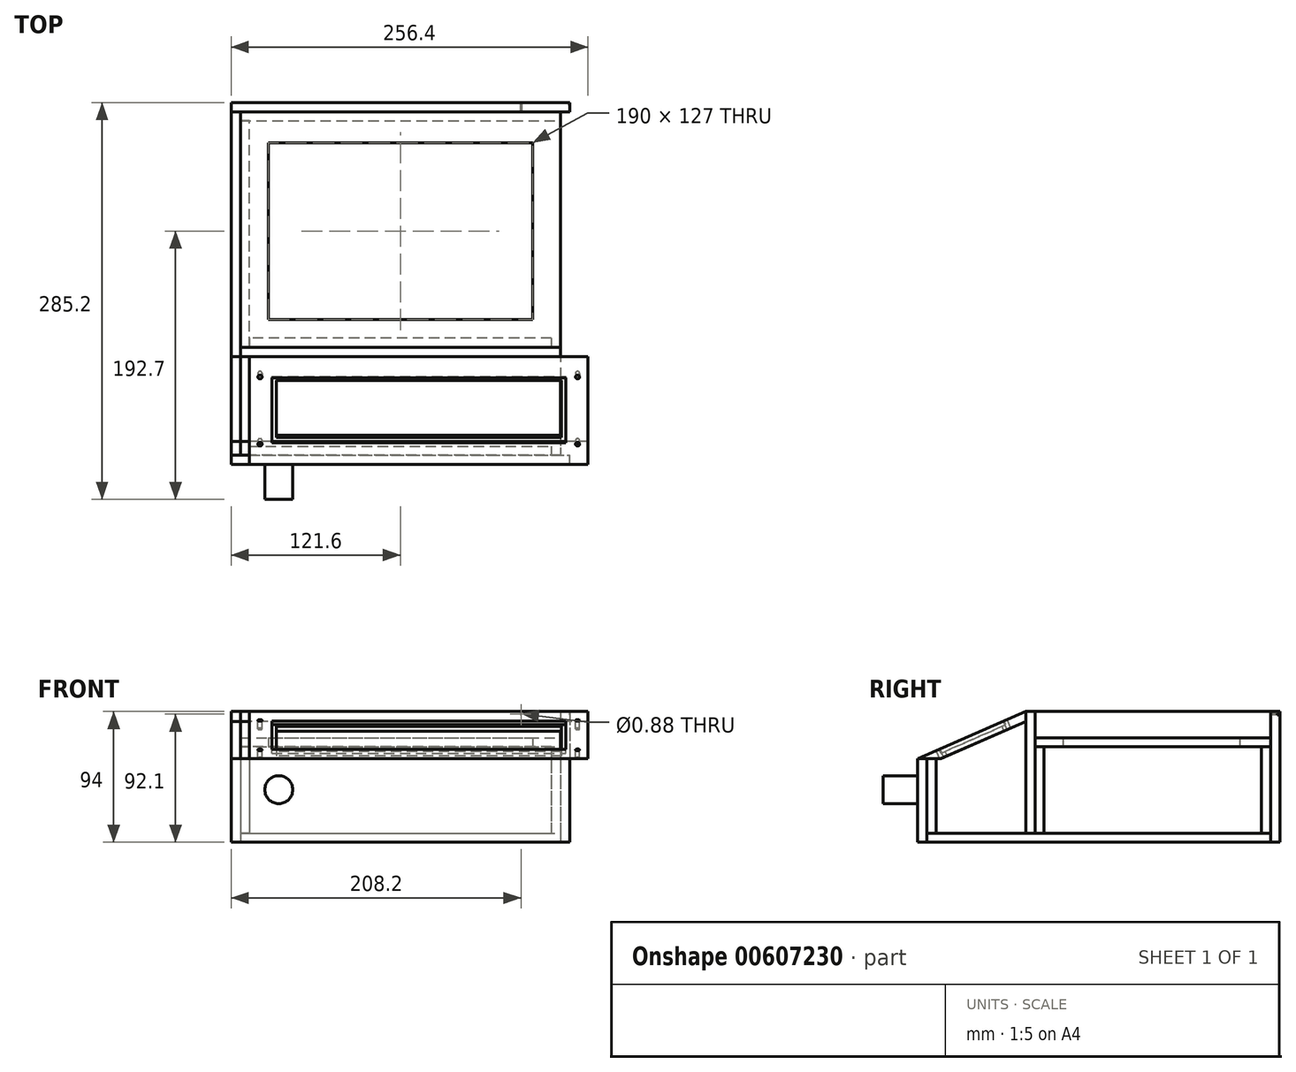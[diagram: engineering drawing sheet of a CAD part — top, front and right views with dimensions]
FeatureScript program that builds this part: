
annotation { "Feature Type Name" : "Feature", "Feature Type Description" : "" }
export const myFeature = defineFeature(function(context is Context, id is Id, definition is map)
    precondition{}
    {
        {
            var Q0;
            Q0=qCreatedBy(makeId("Top.planeOp"),FACE);
            var sketch = newSketch(context, id + "F0", { "sketchPlane" : qUnion([Q0])});
            skLineSegment(sketch, "E0.bottom", {"start": v(115, 123.5) * mm, "end": v(-115, 123.5) * mm});
            skLineSegment(sketch, "E0.top", {"start": v(115, -123.5) * mm, "end": v(-115, -123.5) * mm});
            skLineSegment(sketch, "E0.left", {"start": v(115, 123.5) * mm, "end": v(115, -123.5) * mm});
            skLineSegment(sketch, "E0.right", {"start": v(-115, 123.5) * mm, "end": v(-115, -123.5) * mm});
            skPoint(sketch, "E0.middle", {"position": v(0, 0) * mm});
            skSolve(sketch);
        }
        {
            var Q0;
            Q0 = qSketchRegion(id + "F0", true);
            extrude(context, id + "F1", {"entities" : qUnion([Q0]), "depth" : 6.6 * mm, "offsetDistance" : 25 * mm});
        }
        {
            var Q0;
            Q0=makeQuery(id+"F1.opExtrude","SWEPT_FACE",FACE,{"disambiguationData":[OSD([sQuery(id+"F0.wireOp",EDGE,"E0.bottom")])]});
            var sketch = newSketch(context, id + "F2", { "sketchPlane" : qUnion([Q0])});
            skLineSegment(sketch, "E1.bottom", {"start": v(-121.6, 94) * mm, "end": v(121.6, 94) * mm});
            skLineSegment(sketch, "E1.top", {"start": v(-121.6, 0) * mm, "end": v(121.6, 0) * mm});
            skLineSegment(sketch, "E1.left", {"start": v(-121.6, 94) * mm, "end": v(-121.6, 0) * mm});
            skLineSegment(sketch, "E1.right", {"start": v(121.6, 94) * mm, "end": v(121.6, 0) * mm});
            skCircle(sketch, "E2", {"center": v(-86.6, 92.1) * mm, "radius": 0.44 * mm});
            skSolve(sketch);
        }
        {
            var Q0;
            Q0 = qSketchRegion(id + "F2", true);
            extrude(context, id + "F3", {"entities" : qUnion([Q0]), "depth" : 6.6 * mm, "offsetDistance" : 25 * mm});
        }
        {
            var Q0;
            Q0=makeQuery(id+"F1.opExtrude","SWEPT_FACE",FACE,{"disambiguationData":[OSD([sQuery(id+"F0.wireOp",EDGE,"E0.right")])]});
            var sketch = newSketch(context, id + "F4", { "sketchPlane" : qUnion([Q0])});
            skLineSegment(sketch, "E3.bottom", {"start": v(-123.5, 94) * mm, "end": v(123.5, 94) * mm});
            skLineSegment(sketch, "E3.top", {"start": v(-123.5, 0) * mm, "end": v(123.5, 0) * mm});
            skLineSegment(sketch, "E3.left", {"start": v(-123.5, 94) * mm, "end": v(-123.5, 0) * mm});
            skLineSegment(sketch, "E3.right", {"start": v(123.5, 94) * mm, "end": v(123.5, 0) * mm});
            skSolve(sketch);
        }
        {
            var Q0;
            Q0 = qSketchRegion(id + "F4", true);
            extrude(context, id + "F5", {"entities" : qUnion([Q0]), "depth" : 6.6 * mm, "offsetDistance" : 25 * mm});
        }
        {
            var Q0;
            Q0=makeQuery(id+"F3.opExtrude","CAP_FACE",FACE,{"disambiguationData":[OSD([sQuery(id+"F2.wireOp",EDGE,"E1.bottom"),sQuery(id+"F2.wireOp",EDGE,"E1.top"),sQuery(id+"F2.wireOp",EDGE,"E1.left"),sQuery(id+"F2.wireOp",EDGE,"E1.right")])],"isStart":true});
            var sketch = newSketch(context, id + "F6", { "sketchPlane" : qUnion([Q0])});
            skLineSegment(sketch, "E4.bottom", {"start": v(-115, 68.6) * mm, "end": v(115, 68.6) * mm});
            skLineSegment(sketch, "E4.top", {"start": v(-115, 6.6) * mm, "end": v(115, 6.6) * mm});
            skLineSegment(sketch, "E4.left", {"start": v(-115, 68.6) * mm, "end": v(-115, 6.6) * mm});
            skLineSegment(sketch, "E4.right", {"start": v(115, 68.6) * mm, "end": v(115, 6.6) * mm});
            skSolve(sketch);
        }
        {
            var Q0;
            Q0 = qSketchRegion(id + "F6", true);
            extrude(context, id + "F7", {"entities" : qUnion([Q0]), "depth" : 6.6 * mm, "offsetDistance" : 25 * mm});
        }
        {
            var Q0;
            Q0=makeQuery(id+"F1.opExtrude","SWEPT_FACE",FACE,{"disambiguationData":[OSD([sQuery(id+"F0.wireOp",EDGE,"E0.top")])]});
            var sketch = newSketch(context, id + "F8", { "sketchPlane" : qUnion([Q0])});
            skLineSegment(sketch, "E5.bottom", {"start": v(-121.6, 60) * mm, "end": v(121.6, 60) * mm});
            skLineSegment(sketch, "E5.top", {"start": v(-121.6, 0) * mm, "end": v(121.6, 0) * mm});
            skLineSegment(sketch, "E5.left", {"start": v(-121.6, 60) * mm, "end": v(-121.6, 0) * mm});
            skLineSegment(sketch, "E5.right", {"start": v(121.6, 60) * mm, "end": v(121.6, 0) * mm});
            skSolve(sketch);
        }
        {
            var Q0;
            Q0 = qSketchRegion(id + "F8", true);
            extrude(context, id + "F9", {"entities" : qUnion([Q0]), "depth" : 6.6 * mm, "offsetDistance" : 25 * mm});
        }
        {
            var Q0;
            Q0=makeQuery(id+"F5.opExtrude","CAP_FACE",FACE,{"disambiguationData":[OSD([sQuery(id+"F4.wireOp",EDGE,"E3.bottom"),sQuery(id+"F4.wireOp",EDGE,"E3.top"),sQuery(id+"F4.wireOp",EDGE,"E3.left"),sQuery(id+"F4.wireOp",EDGE,"E3.right")])],"isStart":true});
            var sketch = newSketch(context, id + "F10", { "sketchPlane" : qUnion([Q0])});
            skLineSegment(sketch, "E6.bottom", {"start": v(-123.5, 94) * mm, "end": v(-52.5, 94) * mm});
            skLineSegment(sketch, "E6.top", {"start": v(-123.5, 6.6) * mm, "end": v(-52.5, 6.6) * mm});
            skLineSegment(sketch, "E6.left", {"start": v(-123.5, 94) * mm, "end": v(-123.5, 6.6) * mm});
            skLineSegment(sketch, "E6.right", {"start": v(-52.5, 94) * mm, "end": v(-52.5, 6.6) * mm});
            skSolve(sketch);
        }
        {
            var Q0;
            Q0 = qSketchRegion(id + "F10", true);
            extrude(context, id + "F11", {"entities" : qUnion([Q0]), "depth" : 6.6 * mm, "offsetDistance" : 25 * mm});
        }
        {
            var Q0;
            Q0=makeQuery(id+"F11.opExtrude","SWEPT_FACE",FACE,{"disambiguationData":[OSD([sQuery(id+"F10.wireOp",EDGE,"E6.right")])]});
            var sketch = newSketch(context, id + "F12", { "sketchPlane" : qUnion([Q0])});
            skLineSegment(sketch, "E7.bottom", {"start": v(115, 94) * mm, "end": v(-115, 94) * mm});
            skLineSegment(sketch, "E7.top", {"start": v(115, 6.6) * mm, "end": v(-115, 6.6) * mm});
            skLineSegment(sketch, "E7.left", {"start": v(115, 94) * mm, "end": v(115, 6.6) * mm});
            skLineSegment(sketch, "E7.right", {"start": v(-115, 94) * mm, "end": v(-115, 6.6) * mm});
            skSolve(sketch);
        }
        {
            var Q0;
            Q0 = qSketchRegion(id + "F12", true);
            extrude(context, id + "F13", {"entities" : qUnion([Q0]), "depth" : 6.6 * mm, "offsetDistance" : 25 * mm});
        }
        {
            var Q0;
            Q0=makeQuery(id+"F3.opExtrude","CAP_FACE",FACE,{"disambiguationData":[OSD([sQuery(id+"F2.wireOp",EDGE,"E1.bottom"),sQuery(id+"F2.wireOp",EDGE,"E1.top"),sQuery(id+"F2.wireOp",EDGE,"E1.left"),sQuery(id+"F2.wireOp",EDGE,"E1.right"),sQuery(id+"F2.wireOp",EDGE,"E2")])],"isStart":false});
            var sketch = newSketch(context, id + "F14", { "sketchPlane" : qUnion([Q0])});
            skCircle(sketch, "E8", {"center": v(-121.6, 92.1) * mm, "radius": 0.4 * mm});
            skSolve(sketch);
        }
        {
            var Q0;
            Q0 = qSketchRegion(id + "F14", true);
            extrude(context, id + "F15", {"entities" : qUnion([Q0]), "operationType" : NewBodyOperationType.REMOVE, "oppositeDirection" : true, "depth" : 2 * mm, "offsetDistance" : 25 * mm});
        }
        {
            var Q0;
            Q0=makeQuery(id+"F5.opExtrude","CAP_FACE",FACE,{"disambiguationData":[OSD([sQuery(id+"F4.wireOp",EDGE,"E3.bottom"),sQuery(id+"F4.wireOp",EDGE,"E3.top"),sQuery(id+"F4.wireOp",EDGE,"E3.left"),sQuery(id+"F4.wireOp",EDGE,"E3.right")])],"isStart":true});
            var sketch = newSketch(context, id + "F16", { "sketchPlane" : qUnion([Q0])});
            skLineSegment(sketch, "E9.bottom", {"start": v(-45.9, 68.6) * mm, "end": v(116.9, 68.6) * mm});
            skLineSegment(sketch, "E9.top", {"start": v(-45.9, 6.6) * mm, "end": v(116.9, 6.6) * mm});
            skLineSegment(sketch, "E9.left", {"start": v(-45.9, 68.6) * mm, "end": v(-45.9, 6.6) * mm});
            skLineSegment(sketch, "E9.right", {"start": v(116.9, 68.6) * mm, "end": v(116.9, 6.6) * mm});
            skSolve(sketch);
        }
        {
            var Q0;
            Q0 = qSketchRegion(id + "F16", true);
            extrude(context, id + "F17", {"entities" : qUnion([Q0]), "depth" : 6.6 * mm, "offsetDistance" : 25 * mm});
        }
        {
            var Q0;
            Q0=makeQuery(id+"F13.opExtrude","CAP_FACE",FACE,{"disambiguationData":[OSD([sQuery(id+"F12.wireOp",EDGE,"E7.bottom"),sQuery(id+"F12.wireOp",EDGE,"E7.top"),sQuery(id+"F12.wireOp",EDGE,"E7.left"),sQuery(id+"F12.wireOp",EDGE,"E7.right")])],"isStart":false});
            var sketch = newSketch(context, id + "F18", { "sketchPlane" : qUnion([Q0])});
            skLineSegment(sketch, "E10.bottom", {"start": v(-108.4, 68.6) * mm, "end": v(108.4, 68.6) * mm});
            skLineSegment(sketch, "E10.top", {"start": v(-108.4, 6.6) * mm, "end": v(108.4, 6.6) * mm});
            skLineSegment(sketch, "E10.left", {"start": v(-108.4, 68.6) * mm, "end": v(-108.4, 6.6) * mm});
            skLineSegment(sketch, "E10.right", {"start": v(108.4, 68.6) * mm, "end": v(108.4, 6.6) * mm});
            skSolve(sketch);
        }
        {
            var Q0;
            Q0 = qSketchRegion(id + "F18", true);
            extrude(context, id + "F19", {"entities" : qUnion([Q0]), "depth" : 6.6 * mm, "offsetDistance" : 25 * mm});
        }
        {
            var Q0;
            Q0=makeQuery(id+"F7.opExtrude","SWEPT_FACE",FACE,{"disambiguationData":[OSD([sQuery(id+"F6.wireOp",EDGE,"E4.bottom")])]});
            var sketch = newSketch(context, id + "F20", { "sketchPlane" : qUnion([Q0])});
            skLineSegment(sketch, "E11.bottom", {"start": v(-115, 123.5) * mm, "end": v(115, 123.5) * mm});
            skLineSegment(sketch, "E11.top", {"start": v(-115, -45.9) * mm, "end": v(115, -45.9) * mm});
            skLineSegment(sketch, "E11.left", {"start": v(-115, 123.5) * mm, "end": v(-115, -45.9) * mm});
            skLineSegment(sketch, "E11.right", {"start": v(115, 123.5) * mm, "end": v(115, -45.9) * mm});
            skLineSegment(sketch, "E12.bottom", {"start": v(-95, -25.9) * mm, "end": v(95, -25.9) * mm});
            skLineSegment(sketch, "E12.top", {"start": v(-95, 101.1) * mm, "end": v(95, 101.1) * mm});
            skLineSegment(sketch, "E12.left", {"start": v(-95, -25.9) * mm, "end": v(-95, 101.1) * mm});
            skLineSegment(sketch, "E12.right", {"start": v(95, -25.9) * mm, "end": v(95, 101.1) * mm});
            skSolve(sketch);
        }
        {
            var Q0;
            {var subQ2=sQuery(id+"F20.wireOp",EDGE,"E11.top");Q0=makeQuery(id+"F20.imprint","IMPRINT",FACE,{"disambiguationData":[TD([[makeQuery(id+"F20.imprint","IMPRINT",EDGE,{"derivedFrom":subQ2}),1.0]])]});}
            var Q1;
            {var subQ0=sQuery(id+"F20.wireOp",EDGE,"E11.bottom");Q1=makeQuery(id+"F20.imprint","IMPRINT",FACE,{"disambiguationData":[TD([[makeQuery(id+"F20.imprint","IMPRINT",EDGE,{"derivedFrom":subQ0}),-1.0]])]});}
            extrude(context, id + "F21", {"entities" : qUnion([Q0, Q1]), "depth" : 6.6 * mm, "offsetDistance" : 25 * mm});
        }
        {
            var Q0;
            Q0=makeQuery(id+"F9.opExtrude","CAP_FACE",FACE,{"disambiguationData":[OSD([sQuery(id+"F8.wireOp",EDGE,"E5.bottom"),sQuery(id+"F8.wireOp",EDGE,"E5.top"),sQuery(id+"F8.wireOp",EDGE,"E5.left"),sQuery(id+"F8.wireOp",EDGE,"E5.right")])],"isStart":true});
            var sketch = newSketch(context, id + "F22", { "sketchPlane" : qUnion([Q0])});
            skLineSegment(sketch, "E13.bottom", {"start": v(-108.4, 60) * mm, "end": v(108.4, 60) * mm});
            skLineSegment(sketch, "E13.top", {"start": v(-108.4, 6.6) * mm, "end": v(108.4, 6.6) * mm});
            skLineSegment(sketch, "E13.left", {"start": v(-108.4, 60) * mm, "end": v(-108.4, 6.6) * mm});
            skLineSegment(sketch, "E13.right", {"start": v(108.4, 60) * mm, "end": v(108.4, 6.6) * mm});
            skSolve(sketch);
        }
        {
            var Q0;
            Q0 = qSketchRegion(id + "F22", true);
            extrude(context, id + "F23", {"entities" : qUnion([Q0]), "depth" : 6.6 * mm, "offsetDistance" : 25 * mm});
        }
        {
            var Q0;
            Q0=makeQuery(id+"F11.opExtrude","CAP_FACE",FACE,{"disambiguationData":[OSD([sQuery(id+"F10.wireOp",EDGE,"E6.bottom"),sQuery(id+"F10.wireOp",EDGE,"E6.top"),sQuery(id+"F10.wireOp",EDGE,"E6.left"),sQuery(id+"F10.wireOp",EDGE,"E6.right")])],"isStart":false});
            var sketch = newSketch(context, id + "F24", { "sketchPlane" : qUnion([Q0])});
            skLineSegment(sketch, "E14", {"start": v(-113.4, 60.12) * mm, "end": v(-52.5, 86.8) * mm});
            skLineSegment(sketch, "E15", {"start": v(-52.5, 86.8) * mm, "end": v(-52.5, 94) * mm});
            skLineSegment(sketch, "E16", {"start": v(-52.5, 94) * mm, "end": v(-130, 60.06) * mm});
            skLineSegment(sketch, "E17", {"start": v(-130, 60.06) * mm, "end": v(-113.4, 60.12) * mm});
            skSolve(sketch);
        }
        {
            var Q0;
            {var subQ5=sQuery(id+"F24.wireOp",EDGE,"E14");Q0=makeQuery(id+"F24.imprint","IMPRINT",FACE,{"disambiguationData":[TD([[makeQuery(id+"F24.imprint","IMPRINT",EDGE,{"derivedFrom":subQ5}),1.0]])]});}
            var Q1;
            {var subQ0=sQuery(id+"F24.wireOp",EDGE,"E17");var subQ1=sQuery(id+"F24.wireOp",EDGE,"E16");var subQ2=makeQuery(id+"F24.imprint","INTERSECT",VERTEX,{"derivedFrom":[subQ1,subQ0]});Q1=makeQuery(id+"F24.imprint","IMPRINT",FACE,{"disambiguationData":[TD([[makeQuery(id+"F24.imprint","IMPRINT",EDGE,{"disambiguationData":[TD([[subQ2,1.0]])],"derivedFrom":subQ1}),1.0]])]});}
            extrude(context, id + "F25", {"entities" : qUnion([Q0, Q1]), "depth" : 243.2 * mm, "offsetDistance" : 25 * mm});
        }
        {
            var Q0;
            Q0=makeQuery(id+"F11.opExtrude","CAP_FACE",FACE,{"disambiguationData":[OSD([sQuery(id+"F10.wireOp",EDGE,"E6.bottom"),sQuery(id+"F10.wireOp",EDGE,"E6.top"),sQuery(id+"F10.wireOp",EDGE,"E6.left"),sQuery(id+"F10.wireOp",EDGE,"E6.right")])],"isStart":false});
            var sketch = newSketch(context, id + "F26", { "sketchPlane" : qUnion([Q0])});
            skLineSegment(sketch, "E18", {"start": v(-52.5, 94) * mm, "end": v(-130.02, 60) * mm});
            skLineSegment(sketch, "E19", {"start": v(-130.02, 60) * mm, "end": v(-113.59, 60) * mm});
            skLineSegment(sketch, "E20", {"start": v(-113.59, 60) * mm, "end": v(-52.5, 86.8) * mm});
            skLineSegment(sketch, "E21", {"start": v(-52.5, 86.8) * mm, "end": v(-52.5, 94) * mm});
            skLineSegment(sketch, "E22", {"start": v(-52.5, 94) * mm, "end": v(-123.5, 94) * mm});
            skLineSegment(sketch, "E23", {"start": v(-123.5, 94) * mm, "end": v(-123.5, 62.86) * mm});
            skLineSegment(sketch, "E24", {"start": v(-123.5, 62.86) * mm, "end": v(-52.5, 94) * mm});
            skSolve(sketch);
        }
        {
            var Q0;
            Q0 = qSketchRegion(id + "F26", true);
            extrude(context, id + "F27", {"entities" : qUnion([Q0]), "operationType" : NewBodyOperationType.REMOVE, "oppositeDirection" : true, "depth" : 25 * mm, "offsetDistance" : 25 * mm});
        }
        {
            var Q0;
            Q0 = qSketchRegion(id + "F26", true);
            extrude(context, id + "F28", {"entities" : qUnion([Q0]), "operationType" : NewBodyOperationType.REMOVE, "oppositeDirection" : true, "depth" : 25 * mm, "offsetDistance" : 25 * mm});
        }
        {
            var Q0;
            Q0=makeQuery(id+"F25.opExtrude","SWEPT_FACE",FACE,{"disambiguationData":[OSD([sQuery(id+"F24.wireOp",EDGE,"E14")])]});
            var sketch = newSketch(context, id + "F29", { "sketchPlane" : qUnion([Q0])});
            skLineSegment(sketch, "E25.bottom", {"start": v(115.63, 30.38) * mm, "end": v(-89.23, 30.38) * mm});
            skLineSegment(sketch, "E25.top", {"start": v(115.63, 75.03) * mm, "end": v(-89.23, 75.03) * mm});
            skLineSegment(sketch, "E25.left", {"start": v(115.63, 30.38) * mm, "end": v(115.63, 75.03) * mm});
            skLineSegment(sketch, "E25.right", {"start": v(-89.23, 30.38) * mm, "end": v(-89.23, 75.03) * mm});
            skSolve(sketch);
        }
        {
            var Q0;
            Q0 = qSketchRegion(id + "F29", true);
            extrude(context, id + "F30", {"entities" : qUnion([Q0]), "operationType" : NewBodyOperationType.REMOVE, "endBound" : BoundingType.THROUGH_ALL, "oppositeDirection" : true, "depth" : 3.1 * mm, "offsetDistance" : 25 * mm});
        }
        {
            var Q0;
            Q0=makeQuery(id+"F25.opExtrude","SWEPT_FACE",FACE,{"disambiguationData":[OSD([sQuery(id+"F24.wireOp",EDGE,"E16")])]});
            var sketch = newSketch(context, id + "F31", { "sketchPlane" : qUnion([Q0])});
            skLineSegment(sketch, "E26.bottom", {"start": v(-92.4, -78.19) * mm, "end": v(118.8, -78.19) * mm});
            skLineSegment(sketch, "E26.top", {"start": v(-92.4, -27.19) * mm, "end": v(118.8, -27.19) * mm});
            skLineSegment(sketch, "E26.left", {"start": v(-92.4, -78.19) * mm, "end": v(-92.4, -27.19) * mm});
            skLineSegment(sketch, "E26.right", {"start": v(118.8, -78.19) * mm, "end": v(118.8, -27.19) * mm});
            skSolve(sketch);
        }
        {
            var Q0;
            Q0 = qSketchRegion(id + "F31", true);
            extrude(context, id + "F32", {"entities" : qUnion([Q0]), "operationType" : NewBodyOperationType.REMOVE, "oppositeDirection" : true, "depth" : 3 * mm, "offsetDistance" : 25 * mm});
        }
        {
            var Q0;
            Q0=makeQuery(id+"F25.opExtrude","SWEPT_FACE",FACE,{"disambiguationData":[OSD([sQuery(id+"F24.wireOp",EDGE,"E16")])]});
            var sketch = newSketch(context, id + "F33", { "sketchPlane" : qUnion([Q0])});
            skCircle(sketch, "E27", {"center": v(-100.9, -79.1) * mm, "radius": 1.5 * mm});
            skCircle(sketch, "E28", {"center": v(-100.9, -26.38) * mm, "radius": 1.5 * mm});
            skCircle(sketch, "E29", {"center": v(127.3, -26.38) * mm, "radius": 1.5 * mm});
            skCircle(sketch, "E30", {"center": v(127.3, -79.1) * mm, "radius": 1.5 * mm});
            skSolve(sketch);
        }
        {
            var Q0;
            Q0 = qSketchRegion(id + "F33", true);
            extrude(context, id + "F34", {"entities" : qUnion([Q0]), "operationType" : NewBodyOperationType.REMOVE, "oppositeDirection" : true, "depth" : 6.6 * mm, "offsetDistance" : 25 * mm});
        }
        {
            var Q0;
            Q0=makeQuery(id+"F9.opExtrude","CAP_FACE",FACE,{"disambiguationData":[OSD([sQuery(id+"F8.wireOp",EDGE,"E5.bottom"),sQuery(id+"F8.wireOp",EDGE,"E5.top"),sQuery(id+"F8.wireOp",EDGE,"E5.left"),sQuery(id+"F8.wireOp",EDGE,"E5.right")])],"isStart":false});
            var sketch = newSketch(context, id + "F35", { "sketchPlane" : qUnion([Q0])});
            skCircle(sketch, "E31", {"center": v(-87.4, 37.81) * mm, "radius": 10 * mm});
            skSolve(sketch);
        }
        {
            var Q0;
            Q0 = qSketchRegion(id + "F35", true);
            extrude(context, id + "F36", {"entities" : qUnion([Q0]), "operationType" : NewBodyOperationType.ADD, "depth" : 25 * mm, "offsetDistance" : 25 * mm});
        }
    });
